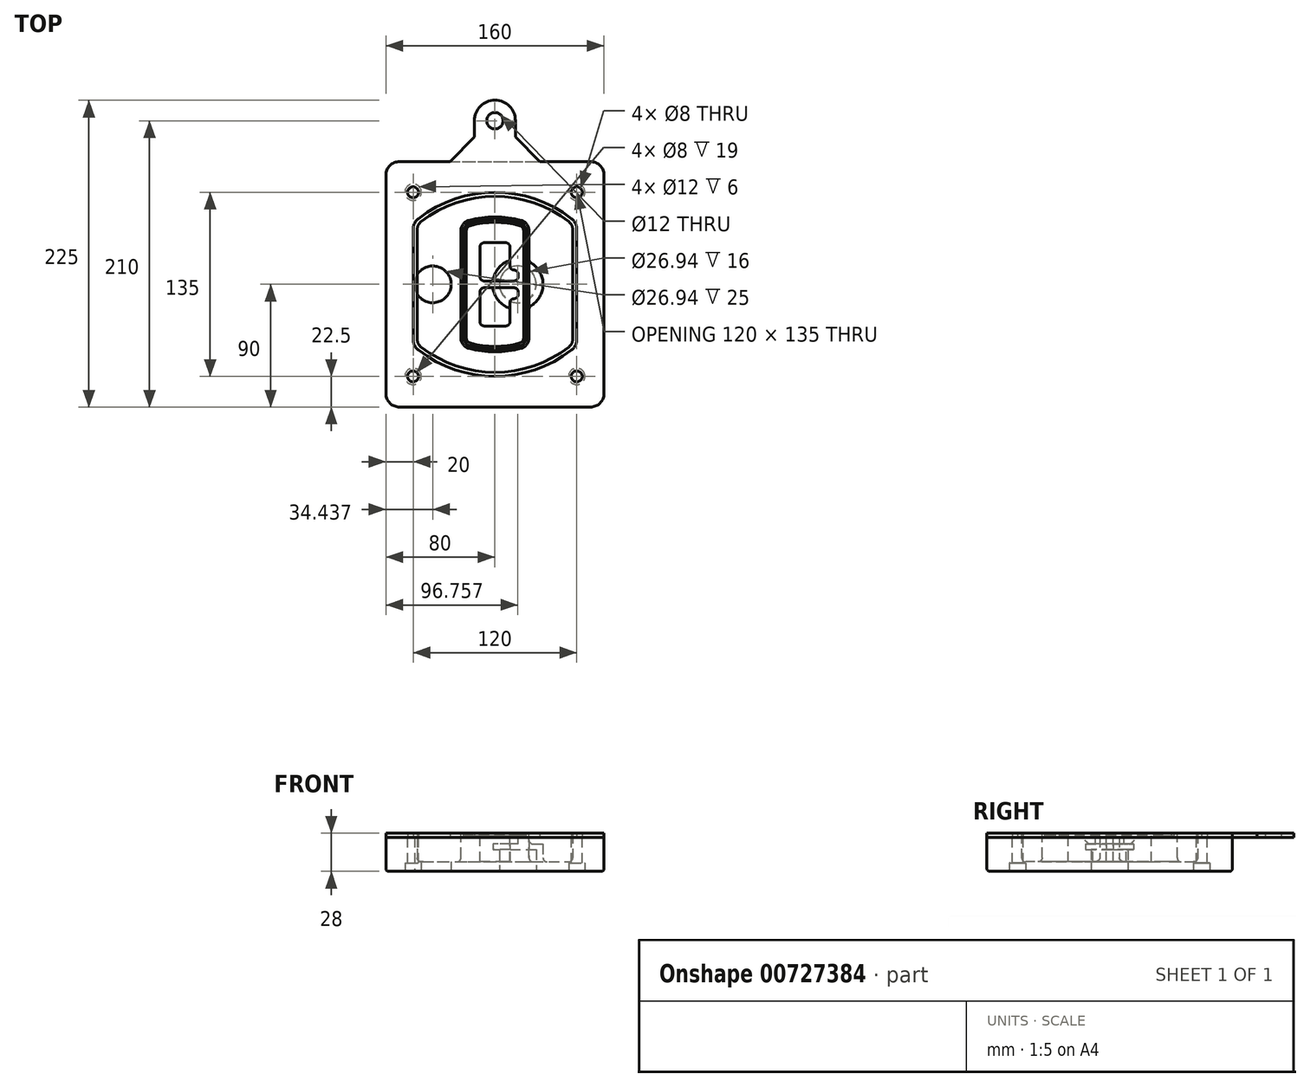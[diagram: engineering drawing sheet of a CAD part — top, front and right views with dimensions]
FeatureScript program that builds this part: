
annotation { "Feature Type Name" : "Feature", "Feature Type Description" : "" }
export const myFeature = defineFeature(function(context is Context, id is Id, definition is map)
    precondition{}
    {
        {
            var Q0;
            Q0=qCreatedBy(makeId("Top.planeOp"),FACE);
            var sketch = newSketch(context, id + "F0", { "sketchPlane" : qUnion([Q0])});
            skPoint(sketch, "E0.rect.middle", {"position": v(0, 0) * mm});
            skLineSegment(sketch, "E1.bottom", {"start": v(-70, -90) * mm, "end": v(70, -90) * mm});
            skLineSegment(sketch, "E1.top", {"start": v(-70, 90) * mm, "end": v(70, 90) * mm});
            skLineSegment(sketch, "E1.left", {"start": v(-80, -80) * mm, "end": v(-80, 80) * mm});
            skLineSegment(sketch, "E1.right", {"start": v(80, -80) * mm, "end": v(80, 80) * mm});
            skLineSegment(sketch, "E2", {"start": v(-80, 90) * mm, "end": v(80, -90) * mm, "construction": true});
            skLineSegment(sketch, "E3", {"start": v(80, 90) * mm, "end": v(-80, -90) * mm, "construction": true});
            skCircle(sketch, "E4", {"center": v(-60, 67.5) * mm, "radius": 4 * mm});
            skCircle(sketch, "E5", {"center": v(60, 67.5) * mm, "radius": 4 * mm});
            skCircle(sketch, "E6", {"center": v(60, -67.5) * mm, "radius": 4 * mm});
            skCircle(sketch, "E7", {"center": v(-60, -67.5) * mm, "radius": 4 * mm});
            skLineSegment(sketch, "E8", {"start": v(-60, 67.5) * mm, "end": v(60, 67.5) * mm, "construction": true});
            skLineSegment(sketch, "E9", {"start": v(60, 67.5) * mm, "end": v(60, -67.5) * mm, "construction": true});
            skLineSegment(sketch, "E10", {"start": v(60, -67.5) * mm, "end": v(-60, -67.5) * mm, "construction": true});
            skLineSegment(sketch, "E11", {"start": v(-60, -67.5) * mm, "end": v(-60, 67.5) * mm, "construction": true});
            skLineSegment(sketch, "E12", {"start": v(-60, 40.3) * mm, "end": v(-60, -40.3) * mm});
            skLineSegment(sketch, "E13", {"start": v(60, 40.3) * mm, "end": v(60, -40.3) * mm});
            skArc(sketch, "E14", {"start": v(56.15, 48.18) * mm, "mid": v(0, 67.5) * mm, "end": v(-56.15, 48.18) * mm});
            skArc(sketch, "E15", {"start": v(-56.15, -48.18) * mm, "mid": v(0, -67.5) * mm, "end": v(56.15, -48.18) * mm});
            skLineSegment(sketch, "E16", {"start": v(-60, 0) * mm, "end": v(60, 0) * mm, "construction": true});
            skPoint(sketch, "E17.visualSharp", {"position": v(-60, -45) * mm});
            skArc(sketch, "E17.filletArc", {"start": v(-60, -40.3) * mm, "mid": v(-58.99, -44.68) * mm, "end": v(-56.15, -48.18) * mm});
            skPoint(sketch, "E18.visualSharp", {"position": v(-60, 45) * mm});
            skArc(sketch, "E18.filletArc", {"start": v(-56.15, 48.18) * mm, "mid": v(-58.99, 44.68) * mm, "end": v(-60, 40.3) * mm});
            skPoint(sketch, "E19.visualSharp", {"position": v(60, 45) * mm});
            skArc(sketch, "E19.filletArc", {"start": v(60, 40.3) * mm, "mid": v(58.99, 44.68) * mm, "end": v(56.15, 48.18) * mm});
            skPoint(sketch, "E20.visualSharp", {"position": v(60, -45) * mm});
            skArc(sketch, "E20.filletArc", {"start": v(56.15, -48.18) * mm, "mid": v(58.99, -44.68) * mm, "end": v(60, -40.3) * mm});
            skPoint(sketch, "E21.visualSharp", {"position": v(-80, 90) * mm});
            skArc(sketch, "E21.filletArc", {"start": v(-70, 90) * mm, "mid": v(-77.07, 87.07) * mm, "end": v(-80, 80) * mm});
            skPoint(sketch, "E22.visualSharp", {"position": v(80, 90) * mm});
            skArc(sketch, "E22.filletArc", {"start": v(80, 80) * mm, "mid": v(77.07, 87.07) * mm, "end": v(70, 90) * mm});
            skPoint(sketch, "E23.visualSharp", {"position": v(80, -90) * mm});
            skArc(sketch, "E23.filletArc", {"start": v(70, -90) * mm, "mid": v(77.07, -87.07) * mm, "end": v(80, -80) * mm});
            skPoint(sketch, "E24.visualSharp", {"position": v(-80, -90) * mm});
            skArc(sketch, "E24.filletArc", {"start": v(-80, -80) * mm, "mid": v(-77.07, -87.07) * mm, "end": v(-70, -90) * mm});
            skArc(sketch, "E25.0", {"start": v(57, 40.3) * mm, "mid": v(56.3, 43.36) * mm, "end": v(54.3, 45.81) * mm});
            skLineSegment(sketch, "E25.1", {"start": v(57, 40.3) * mm, "end": v(57, -40.3) * mm});
            skArc(sketch, "E25.2", {"start": v(54.3, -45.81) * mm, "mid": v(56.3, -43.36) * mm, "end": v(57, -40.3) * mm});
            skArc(sketch, "E25.3", {"start": v(-54.3, -45.81) * mm, "mid": v(0, -64.5) * mm, "end": v(54.3, -45.81) * mm});
            skArc(sketch, "E25.4", {"start": v(-57, -40.3) * mm, "mid": v(-56.3, -43.36) * mm, "end": v(-54.3, -45.81) * mm});
            skArc(sketch, "E25.5", {"start": v(54.3, 45.81) * mm, "mid": v(0, 64.5) * mm, "end": v(-54.3, 45.81) * mm});
            skLineSegment(sketch, "E25.6", {"start": v(-57, 40.3) * mm, "end": v(-57, -40.3) * mm});
            skArc(sketch, "E25.7", {"start": v(-54.3, 45.81) * mm, "mid": v(-56.3, 43.36) * mm, "end": v(-57, 40.3) * mm});
            skArc(sketch, "E26.0", {"start": v(-58.62, 51.33) * mm, "mid": v(-62.58, 46.43) * mm, "end": v(-64, 40.3) * mm});
            skArc(sketch, "E26.1", {"start": v(58.62, 51.33) * mm, "mid": v(0, 71.5) * mm, "end": v(-58.62, 51.33) * mm});
            skArc(sketch, "E26.2", {"start": v(64, 40.3) * mm, "mid": v(62.58, 46.43) * mm, "end": v(58.62, 51.33) * mm});
            skLineSegment(sketch, "E26.3", {"start": v(64, 40.3) * mm, "end": v(64, -40.3) * mm});
            skArc(sketch, "E26.4", {"start": v(58.62, -51.33) * mm, "mid": v(62.58, -46.43) * mm, "end": v(64, -40.3) * mm});
            skLineSegment(sketch, "E26.5", {"start": v(-64, 40.3) * mm, "end": v(-64, -40.3) * mm});
            skArc(sketch, "E26.6", {"start": v(-58.62, -51.33) * mm, "mid": v(0, -71.5) * mm, "end": v(58.62, -51.33) * mm});
            skArc(sketch, "E26.7", {"start": v(-64, -40.3) * mm, "mid": v(-62.58, -46.43) * mm, "end": v(-58.62, -51.33) * mm});
            skSolve(sketch);
        }
        {
            var Q0;
            Q0=makeQuery(id+"F0.imprint","IMPRINT",FACE,{"disambiguationData":[TD([[makeQuery(id+"F0.imprint","IMPRINT",EDGE,{"derivedFrom":sQuery(id+"F0.wireOp",EDGE,"E1.bottom")}),1.0]])]});
            var Q1;
            Q1=makeQuery(id+"F0.imprint","IMPRINT",FACE,{"disambiguationData":[TD([[makeQuery(id+"F0.imprint","IMPRINT",EDGE,{"derivedFrom":sQuery(id+"F0.wireOp",EDGE,"E12")}),1.0]])]});
            var Q2;
            Q2=makeQuery(id+"F0.imprint","IMPRINT",FACE,{"disambiguationData":[TD([[makeQuery(id+"F0.imprint","IMPRINT",EDGE,{"derivedFrom":sQuery(id+"F0.wireOp",EDGE,"E25.0")}),1.0]])]});
            var Q3;
            Q3=makeQuery(id+"F0.imprint","IMPRINT",FACE,{"disambiguationData":[TD([[makeQuery(id+"F0.imprint","IMPRINT",EDGE,{"derivedFrom":sQuery(id+"F0.wireOp",EDGE,"E12")}),-1.0]])]});
            extrude(context, id + "F1", {"entities" : qUnion([Q0, Q1, Q2, Q3]), "oppositeDirection" : true, "depth" : 25 * mm});
        }
        {
            var Q0;
            Q0=makeQuery(id+"F0.imprint","IMPRINT",FACE,{"disambiguationData":[TD([[makeQuery(id+"F0.imprint","IMPRINT",EDGE,{"derivedFrom":sQuery(id+"F0.wireOp",EDGE,"E12")}),1.0]])]});
            extrude(context, id + "F2", {"entities" : qUnion([Q0]), "operationType" : NewBodyOperationType.ADD, "depth" : 3 * mm});
        }
        {
            var Q0;
            Q0=makeQuery(id+"F0.imprint","IMPRINT",FACE,{"disambiguationData":[TD([[makeQuery(id+"F0.imprint","IMPRINT",EDGE,{"derivedFrom":sQuery(id+"F0.wireOp",EDGE,"E25.0")}),1.0]])]});
            extrude(context, id + "F3", {"entities" : qUnion([Q0]), "operationType" : NewBodyOperationType.REMOVE, "oppositeDirection" : true, "depth" : 18 * mm});
        }
        {
            var Q0;
            Q0=makeQuery(id+"F2.opExtrude","CAP_FACE",FACE,{"disambiguationData":[OSD([sQuery(id+"F0.wireOp",EDGE,"E12"),sQuery(id+"F0.wireOp",EDGE,"E13"),sQuery(id+"F0.wireOp",EDGE,"E14"),sQuery(id+"F0.wireOp",EDGE,"E15"),sQuery(id+"F0.wireOp",EDGE,"E17.filletArc"),sQuery(id+"F0.wireOp",EDGE,"E18.filletArc"),sQuery(id+"F0.wireOp",EDGE,"E19.filletArc"),sQuery(id+"F0.wireOp",EDGE,"E20.filletArc"),sQuery(id+"F0.wireOp",EDGE,"E25.0"),sQuery(id+"F0.wireOp",EDGE,"E25.1"),sQuery(id+"F0.wireOp",EDGE,"E25.2"),sQuery(id+"F0.wireOp",EDGE,"E25.3"),sQuery(id+"F0.wireOp",EDGE,"E25.4"),sQuery(id+"F0.wireOp",EDGE,"E25.5"),sQuery(id+"F0.wireOp",EDGE,"E25.6"),sQuery(id+"F0.wireOp",EDGE,"E25.7")])],"isStart":false});
            var sketch = newSketch(context, id + "F4", { "sketchPlane" : qUnion([Q0])});
            skArc(sketch, "E27.0", {"start": v(-19.08, -46.97) * mm, "mid": v(0, -49.5) * mm, "end": v(19.08, -46.97) * mm});
            skArc(sketch, "E28.0", {"start": v(19.08, 46.97) * mm, "mid": v(0, 49.5) * mm, "end": v(-19.08, 46.97) * mm});
            skLineSegment(sketch, "E29", {"start": v(-25, 39.25) * mm, "end": v(-25, -39.25) * mm});
            skLineSegment(sketch, "E30", {"start": v(25, 39.25) * mm, "end": v(25, -39.25) * mm});
            skLineSegment(sketch, "E31", {"start": v(-25, 45.1) * mm, "end": v(25, 45.1) * mm, "construction": true});
            skLineSegment(sketch, "E32", {"start": v(-25, -45.1) * mm, "end": v(25, -45.1) * mm, "construction": true});
            skPoint(sketch, "E33.visualSharp", {"position": v(-25, 45.1) * mm});
            skArc(sketch, "E33.filletArc", {"start": v(-19.08, 46.97) * mm, "mid": v(-23.35, 44.11) * mm, "end": v(-25, 39.25) * mm});
            skPoint(sketch, "E34.visualSharp", {"position": v(25, 45.1) * mm});
            skArc(sketch, "E34.filletArc", {"start": v(25, 39.25) * mm, "mid": v(23.35, 44.11) * mm, "end": v(19.08, 46.97) * mm});
            skPoint(sketch, "E35.visualSharp", {"position": v(25, -45.1) * mm});
            skArc(sketch, "E35.filletArc", {"start": v(19.08, -46.97) * mm, "mid": v(23.35, -44.11) * mm, "end": v(25, -39.25) * mm});
            skPoint(sketch, "E36.visualSharp", {"position": v(-25, -45.1) * mm});
            skArc(sketch, "E36.filletArc", {"start": v(-25, -39.25) * mm, "mid": v(-23.35, -44.11) * mm, "end": v(-19.08, -46.97) * mm});
            skArc(sketch, "E37.0", {"start": v(54.3, 45.81) * mm, "mid": v(0, 64.5) * mm, "end": v(-54.3, 45.81) * mm});
            skArc(sketch, "E37.1", {"start": v(-54.3, 45.81) * mm, "mid": v(-56.3, 43.36) * mm, "end": v(-57, 40.3) * mm});
            skLineSegment(sketch, "E37.2", {"start": v(-57, 40.3) * mm, "end": v(-57, -40.3) * mm});
            skArc(sketch, "E37.3", {"start": v(-57, -40.3) * mm, "mid": v(-56.3, -43.36) * mm, "end": v(-54.3, -45.81) * mm});
            skArc(sketch, "E37.4", {"start": v(-54.3, -45.81) * mm, "mid": v(0, -64.5) * mm, "end": v(54.3, -45.81) * mm});
            skArc(sketch, "E37.5", {"start": v(54.3, -45.81) * mm, "mid": v(56.3, -43.36) * mm, "end": v(57, -40.3) * mm});
            skLineSegment(sketch, "E37.6", {"start": v(57, 40.3) * mm, "end": v(57, -40.3) * mm});
            skArc(sketch, "E37.7", {"start": v(57, 40.3) * mm, "mid": v(56.3, 43.36) * mm, "end": v(54.3, 45.81) * mm});
            skLineSegment(sketch, "E38.0", {"start": v(23, 39.25) * mm, "end": v(23, -39.25) * mm});
            skArc(sketch, "E38.1", {"start": v(18.56, -45.04) * mm, "mid": v(21.76, -42.9) * mm, "end": v(23, -39.25) * mm});
            skArc(sketch, "E38.2", {"start": v(-18.56, -45.04) * mm, "mid": v(0, -47.5) * mm, "end": v(18.56, -45.04) * mm});
            skArc(sketch, "E38.3", {"start": v(-23, -39.25) * mm, "mid": v(-21.76, -42.9) * mm, "end": v(-18.56, -45.04) * mm});
            skLineSegment(sketch, "E38.4", {"start": v(-23, 39.25) * mm, "end": v(-23, -39.25) * mm});
            skArc(sketch, "E38.5", {"start": v(23, 39.25) * mm, "mid": v(21.76, 42.9) * mm, "end": v(18.56, 45.04) * mm});
            skArc(sketch, "E38.6", {"start": v(-18.56, 45.04) * mm, "mid": v(-21.76, 42.9) * mm, "end": v(-23, 39.25) * mm});
            skArc(sketch, "E38.7", {"start": v(18.56, 45.04) * mm, "mid": v(0, 47.5) * mm, "end": v(-18.56, 45.04) * mm});
            skArc(sketch, "E39.0", {"start": v(21, 39.25) * mm, "mid": v(20.18, 41.68) * mm, "end": v(18.04, 43.1) * mm});
            skLineSegment(sketch, "E39.1", {"start": v(21, 39.25) * mm, "end": v(21, -39.25) * mm});
            skArc(sketch, "E39.2", {"start": v(18.04, -43.1) * mm, "mid": v(20.18, -41.68) * mm, "end": v(21, -39.25) * mm});
            skArc(sketch, "E39.3", {"start": v(-18.04, -43.1) * mm, "mid": v(0, -45.5) * mm, "end": v(18.04, -43.1) * mm});
            skArc(sketch, "E39.4", {"start": v(-21, -39.25) * mm, "mid": v(-20.18, -41.68) * mm, "end": v(-18.04, -43.1) * mm});
            skArc(sketch, "E39.5", {"start": v(18.04, 43.1) * mm, "mid": v(0, 45.5) * mm, "end": v(-18.04, 43.1) * mm});
            skLineSegment(sketch, "E39.6", {"start": v(-21, 39.25) * mm, "end": v(-21, -39.25) * mm});
            skArc(sketch, "E39.7", {"start": v(-18.04, 43.1) * mm, "mid": v(-20.18, 41.68) * mm, "end": v(-21, 39.25) * mm});
            skLineSegment(sketch, "E40", {"start": v(-25, 0) * mm, "end": v(25, 0) * mm, "construction": true});
            skLineSegment(sketch, "E41", {"start": v(-11, 5.5) * mm, "end": v(-11, 27.5) * mm});
            skLineSegment(sketch, "E42", {"start": v(-8, 30.5) * mm, "end": v(8, 30.5) * mm});
            skLineSegment(sketch, "E43", {"start": v(11, 27.5) * mm, "end": v(11, 13.5) * mm});
            skLineSegment(sketch, "E44", {"start": v(14, 10.5) * mm, "end": v(14, 10.5) * mm});
            skLineSegment(sketch, "E45", {"start": v(17, 7.5) * mm, "end": v(17, 5.5) * mm});
            skLineSegment(sketch, "E46", {"start": v(14, 2.5) * mm, "end": v(-8, 2.5) * mm});
            skPoint(sketch, "E47.visualSharp", {"position": v(-11, 30.5) * mm});
            skArc(sketch, "E47.filletArc", {"start": v(-8, 30.5) * mm, "mid": v(-10.12, 29.62) * mm, "end": v(-11, 27.5) * mm});
            skPoint(sketch, "E48.visualSharp", {"position": v(11, 30.5) * mm});
            skArc(sketch, "E48.filletArc", {"start": v(11, 27.5) * mm, "mid": v(10.12, 29.62) * mm, "end": v(8, 30.5) * mm});
            skPoint(sketch, "E49.visualSharp", {"position": v(11, 10.5) * mm});
            skArc(sketch, "E49.filletArc", {"start": v(11, 13.5) * mm, "mid": v(11.88, 11.38) * mm, "end": v(14, 10.5) * mm});
            skPoint(sketch, "E50.visualSharp", {"position": v(17, 10.5) * mm});
            skArc(sketch, "E50.filletArc", {"start": v(17, 7.5) * mm, "mid": v(16.12, 9.62) * mm, "end": v(14, 10.5) * mm});
            skPoint(sketch, "E51.visualSharp", {"position": v(17, 2.5) * mm});
            skArc(sketch, "E51.filletArc", {"start": v(14, 2.5) * mm, "mid": v(16.12, 3.38) * mm, "end": v(17, 5.5) * mm});
            skPoint(sketch, "E52.visualSharp", {"position": v(-11, 2.5) * mm});
            skArc(sketch, "E52.filletArc", {"start": v(-11, 5.5) * mm, "mid": v(-10.12, 3.38) * mm, "end": v(-8, 2.5) * mm});
            skLineSegment(sketch, "E53.0.MirrorCS", {"start": v(14, -2.5) * mm, "end": v(-8, -2.5) * mm});
            skArc(sketch, "E54.0.MirrorCS", {"start": v(-11, -5.5) * mm, "mid": v(-10.12, -3.38) * mm, "end": v(-8, -2.5) * mm});
            skLineSegment(sketch, "E55.0.MirrorCS", {"start": v(-11, -5.5) * mm, "end": v(-11, -27.5) * mm});
            skArc(sketch, "E56.0.MirrorCS", {"start": v(-8, -30.5) * mm, "mid": v(-10.12, -29.62) * mm, "end": v(-11, -27.5) * mm});
            skLineSegment(sketch, "E57.0.MirrorCS", {"start": v(-8, -30.5) * mm, "end": v(8, -30.5) * mm});
            skArc(sketch, "E58.0.MirrorCS", {"start": v(11, -27.5) * mm, "mid": v(10.12, -29.62) * mm, "end": v(8, -30.5) * mm});
            skLineSegment(sketch, "E59.0.MirrorCS", {"start": v(11, -27.5) * mm, "end": v(11, -13.5) * mm});
            skArc(sketch, "E60.0.MirrorCS", {"start": v(11, -13.5) * mm, "mid": v(11.88, -11.38) * mm, "end": v(14, -10.5) * mm});
            skArc(sketch, "E61.0.MirrorCS", {"start": v(17, -7.5) * mm, "mid": v(16.12, -9.62) * mm, "end": v(14, -10.5) * mm});
            skLineSegment(sketch, "E62.0.MirrorCS", {"start": v(17, -7.5) * mm, "end": v(17, -5.5) * mm});
            skArc(sketch, "E63.0.MirrorCS", {"start": v(14, -2.5) * mm, "mid": v(16.12, -3.38) * mm, "end": v(17, -5.5) * mm});
            skSolve(sketch);
        }
        {
            var Q0;
            Q0=makeQuery(id+"F4.imprint","IMPRINT",FACE,{"disambiguationData":[TD([[makeQuery(id+"F4.imprint","IMPRINT",EDGE,{"derivedFrom":sQuery(id+"F4.wireOp",EDGE,"E27.0")}),1.0]])]});
            var Q1;
            Q1=makeQuery(id+"F4.imprint","IMPRINT",FACE,{"disambiguationData":[TD([[makeQuery(id+"F4.imprint","IMPRINT",EDGE,{"derivedFrom":sQuery(id+"F4.wireOp",EDGE,"E38.0")}),-1.0]])]});
            var Q2;
            Q2=makeQuery(id+"F4.imprint","IMPRINT",FACE,{"disambiguationData":[TD([[makeQuery(id+"F4.imprint","IMPRINT",EDGE,{"derivedFrom":sQuery(id+"F4.wireOp",EDGE,"E39.0")}),1.0]])]});
            extrude(context, id + "F5", {"entities" : qUnion([Q0, Q1, Q2]), "operationType" : NewBodyOperationType.ADD, "endBound" : BoundingType.UP_TO_NEXT, "oppositeDirection" : true, "depth" : 25 * mm});
        }
        {
            var Q0;
            Q0=makeQuery(id+"F4.imprint","IMPRINT",FACE,{"disambiguationData":[TD([[makeQuery(id+"F4.imprint","IMPRINT",EDGE,{"derivedFrom":sQuery(id+"F4.wireOp",EDGE,"E38.0")}),-1.0]])]});
            extrude(context, id + "F6", {"entities" : qUnion([Q0]), "operationType" : NewBodyOperationType.REMOVE, "oppositeDirection" : true, "depth" : 2 * mm});
        }
        {
            var Q0;
            Q0=makeQuery(id+"F1.opExtrude","CAP_FACE",FACE,{"disambiguationData":[OSD([sQuery(id+"F0.wireOp",EDGE,"E1.bottom"),sQuery(id+"F0.wireOp",EDGE,"E1.top"),sQuery(id+"F0.wireOp",EDGE,"E1.left"),sQuery(id+"F0.wireOp",EDGE,"E1.right"),sQuery(id+"F0.wireOp",EDGE,"E4"),sQuery(id+"F0.wireOp",EDGE,"E5"),sQuery(id+"F0.wireOp",EDGE,"E6"),sQuery(id+"F0.wireOp",EDGE,"E7"),sQuery(id+"F0.wireOp",EDGE,"E21.filletArc"),sQuery(id+"F0.wireOp",EDGE,"E22.filletArc"),sQuery(id+"F0.wireOp",EDGE,"E23.filletArc"),sQuery(id+"F0.wireOp",EDGE,"E24.filletArc")])],"isStart":false});
            var sketch = newSketch(context, id + "F7", { "sketchPlane" : qUnion([Q0])});
            skCircle(sketch, "E64", {"center": v(16.76, 0) * mm, "radius": 13.47 * mm});
            skCircle(sketch, "E65", {"center": v(-45.56, 0) * mm, "radius": 13.47 * mm});
            skLineSegment(sketch, "E66", {"start": v(80, 0) * mm, "end": v(-80, 0) * mm});
            skCircle(sketch, "E67", {"center": v(16.76, 0) * mm, "radius": 18.47 * mm});
            skCircle(sketch, "E68", {"center": v(60, -67.5) * mm, "radius": 6 * mm});
            skCircle(sketch, "E69", {"center": v(-60, -67.5) * mm, "radius": 6 * mm});
            skCircle(sketch, "E70", {"center": v(-60, 67.5) * mm, "radius": 6 * mm});
            skCircle(sketch, "E71", {"center": v(60, 67.5) * mm, "radius": 6 * mm});
            skSolve(sketch);
        }
        {
            var Q0;
            {var subQ1=sQuery(id+"F7.wireOp",EDGE,"E66");var subQ4=sQuery(id+"F7.wireOp",EDGE,"E64");var subQ6=makeQuery(id+"F7.imprint","INTERSECT",VERTEX,{"disambiguationData":[OD(0.0)],"derivedFrom":[subQ4,subQ1]});Q0=makeQuery(id+"F7.imprint","IMPRINT",FACE,{"disambiguationData":[TD([[makeQuery(id+"F7.imprint","IMPRINT",EDGE,{"disambiguationData":[TD([[subQ6,-1.0]])],"derivedFrom":subQ4}),-1.0]])]});}
            var Q1;
            {var subQ0=sQuery(id+"F7.wireOp",EDGE,"E66");var subQ1=sQuery(id+"F7.wireOp",EDGE,"E64");var subQ3=makeQuery(id+"F7.imprint","INTERSECT",VERTEX,{"disambiguationData":[OD(0.0)],"derivedFrom":[subQ1,subQ0]});Q1=makeQuery(id+"F7.imprint","IMPRINT",FACE,{"disambiguationData":[TD([[makeQuery(id+"F7.imprint","IMPRINT",EDGE,{"disambiguationData":[TD([[subQ3,-1.0]])],"derivedFrom":subQ1}),1.0]])]});}
            var Q2;
            {var subQ0=sQuery(id+"F7.wireOp",EDGE,"E66");var subQ1=sQuery(id+"F7.wireOp",EDGE,"E64");var subQ3=makeQuery(id+"F7.imprint","INTERSECT",VERTEX,{"disambiguationData":[OD(0.0)],"derivedFrom":[subQ1,subQ0]});Q2=makeQuery(id+"F7.imprint","IMPRINT",FACE,{"disambiguationData":[TD([[makeQuery(id+"F7.imprint","IMPRINT",EDGE,{"disambiguationData":[TD([[subQ3,1.0]])],"derivedFrom":subQ1}),1.0]])]});}
            var Q3;
            {var subQ1=sQuery(id+"F7.wireOp",EDGE,"E66");var subQ4=sQuery(id+"F7.wireOp",EDGE,"E64");var subQ6=makeQuery(id+"F7.imprint","INTERSECT",VERTEX,{"disambiguationData":[OD(0.0)],"derivedFrom":[subQ4,subQ1]});Q3=makeQuery(id+"F7.imprint","IMPRINT",FACE,{"disambiguationData":[TD([[makeQuery(id+"F7.imprint","IMPRINT",EDGE,{"disambiguationData":[TD([[subQ6,1.0]])],"derivedFrom":subQ4}),-1.0]])]});}
            extrude(context, id + "F8", {"entities" : qUnion([Q0, Q1, Q2, Q3]), "operationType" : NewBodyOperationType.ADD, "oppositeDirection" : true, "depth" : 20 * mm});
        }
        {
            var Q0;
            {var subQ0=sQuery(id+"F7.wireOp",EDGE,"E66");var subQ1=sQuery(id+"F7.wireOp",EDGE,"E64");var subQ3=makeQuery(id+"F7.imprint","INTERSECT",VERTEX,{"disambiguationData":[OD(0.0)],"derivedFrom":[subQ1,subQ0]});Q0=makeQuery(id+"F7.imprint","IMPRINT",FACE,{"disambiguationData":[TD([[makeQuery(id+"F7.imprint","IMPRINT",EDGE,{"disambiguationData":[TD([[subQ3,-1.0]])],"derivedFrom":subQ1}),1.0]])]});}
            var Q1;
            {var subQ0=sQuery(id+"F7.wireOp",EDGE,"E66");var subQ1=sQuery(id+"F7.wireOp",EDGE,"E64");var subQ3=makeQuery(id+"F7.imprint","INTERSECT",VERTEX,{"disambiguationData":[OD(0.0)],"derivedFrom":[subQ1,subQ0]});Q1=makeQuery(id+"F7.imprint","IMPRINT",FACE,{"disambiguationData":[TD([[makeQuery(id+"F7.imprint","IMPRINT",EDGE,{"disambiguationData":[TD([[subQ3,1.0]])],"derivedFrom":subQ1}),1.0]])]});}
            extrude(context, id + "F9", {"entities" : qUnion([Q0, Q1]), "operationType" : NewBodyOperationType.REMOVE, "oppositeDirection" : true, "depth" : 16 * mm});
        }
        {
            var Q0;
            {var subQ0=sQuery(id+"F7.wireOp",EDGE,"E66");var subQ1=sQuery(id+"F7.wireOp",EDGE,"E65");var subQ3=makeQuery(id+"F7.imprint","INTERSECT",VERTEX,{"disambiguationData":[OD(0.0)],"derivedFrom":[subQ1,subQ0]});Q0=makeQuery(id+"F7.imprint","IMPRINT",FACE,{"disambiguationData":[TD([[makeQuery(id+"F7.imprint","IMPRINT",EDGE,{"disambiguationData":[TD([[subQ3,-1.0]])],"derivedFrom":subQ1}),1.0]])]});}
            var Q1;
            {var subQ0=sQuery(id+"F7.wireOp",EDGE,"E66");var subQ1=sQuery(id+"F7.wireOp",EDGE,"E65");var subQ3=makeQuery(id+"F7.imprint","INTERSECT",VERTEX,{"disambiguationData":[OD(0.0)],"derivedFrom":[subQ1,subQ0]});Q1=makeQuery(id+"F7.imprint","IMPRINT",FACE,{"disambiguationData":[TD([[makeQuery(id+"F7.imprint","IMPRINT",EDGE,{"disambiguationData":[TD([[subQ3,1.0]])],"derivedFrom":subQ1}),1.0]])]});}
            extrude(context, id + "F10", {"entities" : qUnion([Q0, Q1]), "operationType" : NewBodyOperationType.REMOVE, "oppositeDirection" : true, "depth" : 25 * mm});
        }
        {
            var Q0;
            Q0=makeQuery(id+"F7.imprint","IMPRINT",FACE,{"disambiguationData":[TD([[makeQuery(id+"F7.imprint","IMPRINT",EDGE,{"derivedFrom":sQuery(id+"F7.wireOp",EDGE,"E68")}),1.0]])]});
            var Q1;
            Q1=makeQuery(id+"F7.imprint","IMPRINT",FACE,{"disambiguationData":[TD([[makeQuery(id+"F7.imprint","IMPRINT",EDGE,{"derivedFrom":makeQuery(id+"F1.opExtrude","CAP_EDGE",EDGE,{"disambiguationData":[OSD([sQuery(id+"F0.wireOp",EDGE,"E5")])],"isStart":false})}),-1.0]])]});
            var Q2;
            Q2=makeQuery(id+"F7.imprint","IMPRINT",FACE,{"disambiguationData":[TD([[makeQuery(id+"F7.imprint","IMPRINT",EDGE,{"derivedFrom":sQuery(id+"F7.wireOp",EDGE,"E69")}),1.0]])]});
            var Q3;
            Q3=makeQuery(id+"F7.imprint","IMPRINT",FACE,{"disambiguationData":[TD([[makeQuery(id+"F7.imprint","IMPRINT",EDGE,{"derivedFrom":makeQuery(id+"F1.opExtrude","CAP_EDGE",EDGE,{"disambiguationData":[OSD([sQuery(id+"F0.wireOp",EDGE,"E4")])],"isStart":false})}),-1.0]])]});
            var Q4;
            Q4=makeQuery(id+"F7.imprint","IMPRINT",FACE,{"disambiguationData":[TD([[makeQuery(id+"F7.imprint","IMPRINT",EDGE,{"derivedFrom":sQuery(id+"F7.wireOp",EDGE,"E70")}),1.0]])]});
            var Q5;
            Q5=makeQuery(id+"F7.imprint","IMPRINT",FACE,{"disambiguationData":[TD([[makeQuery(id+"F7.imprint","IMPRINT",EDGE,{"derivedFrom":makeQuery(id+"F1.opExtrude","CAP_EDGE",EDGE,{"disambiguationData":[OSD([sQuery(id+"F0.wireOp",EDGE,"E7")])],"isStart":false})}),-1.0]])]});
            var Q6;
            Q6=makeQuery(id+"F7.imprint","IMPRINT",FACE,{"disambiguationData":[TD([[makeQuery(id+"F7.imprint","IMPRINT",EDGE,{"derivedFrom":sQuery(id+"F7.wireOp",EDGE,"E71")}),1.0]])]});
            var Q7;
            Q7=makeQuery(id+"F7.imprint","IMPRINT",FACE,{"disambiguationData":[TD([[makeQuery(id+"F7.imprint","IMPRINT",EDGE,{"derivedFrom":makeQuery(id+"F1.opExtrude","CAP_EDGE",EDGE,{"disambiguationData":[OSD([sQuery(id+"F0.wireOp",EDGE,"E6")])],"isStart":false})}),-1.0]])]});
            extrude(context, id + "F11", {"entities" : qUnion([Q0, Q1, Q2, Q3, Q4, Q5, Q6, Q7]), "operationType" : NewBodyOperationType.REMOVE, "oppositeDirection" : true, "depth" : 6 * mm});
        }
        {
            var Q0;
            Q0=makeQuery(id+"F9.boolean.opBoolean","COPY",FACE,{"derivedFrom":makeQuery(id+"F9.opExtrude","CAP_FACE",FACE,{"disambiguationData":[OSD([sQuery(id+"F7.wireOp",EDGE,"E64")])],"isStart":false})});
            var sketch = newSketch(context, id + "F12", { "sketchPlane" : qUnion([Q0])});
            skArc(sketch, "E72.0", {"start": v(11, 17.55) * mm, "mid": v(2.57, 11.82) * mm, "end": v(-1.54, 2.5) * mm});
            skArc(sketch, "E72.1", {"start": v(-1.54, -2.5) * mm, "mid": v(2.57, -11.82) * mm, "end": v(11, -17.55) * mm});
            skLineSegment(sketch, "E73", {"start": v(-1.54, -2.5) * mm, "end": v(14, -2.5) * mm});
            skLineSegment(sketch, "E74.0", {"start": v(14, 2.5) * mm, "end": v(-1.54, 2.5) * mm});
            skArc(sketch, "E74.1", {"start": v(14, 2.5) * mm, "mid": v(16.12, 3.38) * mm, "end": v(17, 5.5) * mm});
            skLineSegment(sketch, "E74.2", {"start": v(17, 7.5) * mm, "end": v(17, 5.5) * mm});
            skArc(sketch, "E74.3", {"start": v(17, 7.5) * mm, "mid": v(16.12, 9.62) * mm, "end": v(14, 10.5) * mm});
            skArc(sketch, "E74.4", {"start": v(11, 13.5) * mm, "mid": v(11.88, 11.38) * mm, "end": v(14, 10.5) * mm});
            skLineSegment(sketch, "E74.5", {"start": v(11, 17.55) * mm, "end": v(11, 13.5) * mm});
            skLineSegment(sketch, "E74.7", {"start": v(14, -2.5) * mm, "end": v(-1.54, -2.5) * mm});
            skArc(sketch, "E74.8", {"start": v(14, -2.5) * mm, "mid": v(16.12, -3.38) * mm, "end": v(17, -5.5) * mm});
            skLineSegment(sketch, "E74.9", {"start": v(17, -7.5) * mm, "end": v(17, -5.5) * mm});
            skArc(sketch, "E74.10", {"start": v(17, -7.5) * mm, "mid": v(16.12, -9.62) * mm, "end": v(14, -10.5) * mm});
            skArc(sketch, "E74.11", {"start": v(11, -13.5) * mm, "mid": v(11.88, -11.38) * mm, "end": v(14, -10.5) * mm});
            skLineSegment(sketch, "E74.12", {"start": v(11, -17.55) * mm, "end": v(11, -13.5) * mm});
            skPoint(sketch, "E75.orphan", {"position": v(11, -27.5) * mm});
            skPoint(sketch, "E76.orphan", {"position": v(-8, -2.5) * mm});
            skPoint(sketch, "E77.orphan", {"position": v(-8, 2.5) * mm});
            skPoint(sketch, "E78.orphan", {"position": v(11, 27.5) * mm});
            skSolve(sketch);
        }
        {
            var Q0;
            {var subQ7=sQuery(id+"F12.wireOp",EDGE,"E72.0");var subQ14=sQuery(id+"F12.wireOp",EDGE,"E72.1");var subQ16=sQuery(id+"F12.wireOp",EDGE,"E74.1");var subQ18=sQuery(id+"F12.wireOp",EDGE,"E74.8");Q0=qUnion([makeQuery(id+"F12.imprint","IMPRINT",FACE,{"disambiguationData":[TD([[makeQuery(id+"F12.imprint","IMPRINT",EDGE,{"derivedFrom":subQ7}),1.0]])]}),makeQuery(id+"F12.imprint","IMPRINT",FACE,{"disambiguationData":[TD([[makeQuery(id+"F12.imprint","IMPRINT",EDGE,{"derivedFrom":subQ14}),1.0]])]}),makeQuery(id+"F12.imprint","IMPRINT",FACE,{"disambiguationData":[TD([[makeQuery(id+"F12.imprint","IMPRINT",EDGE,{"derivedFrom":subQ16}),1.0]])]}),makeQuery(id+"F12.imprint","IMPRINT",FACE,{"disambiguationData":[TD([[makeQuery(id+"F12.imprint","IMPRINT",EDGE,{"derivedFrom":subQ18}),-1.0]])]})]);}
            var Q1;
            Q1=makeQuery(id+"F5.boolean.opBoolean","SPLIT",FACE,{"disambiguationData":[TD([makeQuery(id+"F5.opExtrude","SWEPT_FACE",FACE,{"disambiguationData":[OSD([sQuery(id+"F4.wireOp",EDGE,"E41")])]})])],"derivedFrom":makeQuery(id+"F3.boolean.opBoolean","COPY",FACE,{"derivedFrom":makeQuery(id+"F3.opExtrude","CAP_FACE",FACE,{"disambiguationData":[OSD([sQuery(id+"F0.wireOp",EDGE,"E25.0"),sQuery(id+"F0.wireOp",EDGE,"E25.1"),sQuery(id+"F0.wireOp",EDGE,"E25.2"),sQuery(id+"F0.wireOp",EDGE,"E25.3"),sQuery(id+"F0.wireOp",EDGE,"E25.4"),sQuery(id+"F0.wireOp",EDGE,"E25.5"),sQuery(id+"F0.wireOp",EDGE,"E25.6"),sQuery(id+"F0.wireOp",EDGE,"E25.7")])],"isStart":false})})});
            extrude(context, id + "F13", {"entities" : qUnion([Q0]), "operationType" : NewBodyOperationType.REMOVE, "endBound" : BoundingType.UP_TO_SURFACE, "endBoundEntityFace" : qUnion([Q1]), "depth" : 25 * mm});
        }
        {
            var Q0;
            Q0=makeQuery(id+"F3.boolean.opBoolean","COPY",EDGE,{"derivedFrom":makeQuery(id+"F3.opExtrude","CAP_EDGE",EDGE,{"disambiguationData":[OSD([sQuery(id+"F0.wireOp",EDGE,"E25.6")])],"isStart":false})});
            var Q1;
            Q1=makeQuery(id+"F8.boolean.opBoolean","INTERSECT",EDGE,{"derivedFrom":[makeQuery(id+"F5.opExtrude","SWEPT_FACE",FACE,{"disambiguationData":[OSD([sQuery(id+"F4.wireOp",EDGE,"E30")])]}),makeQuery(id+"F8.opExtrude","CAP_FACE",FACE,{"disambiguationData":[OSD([sQuery(id+"F7.wireOp",EDGE,"E67")])],"isStart":false})]});
            var Q2;
            Q2=makeQuery(id+"F8.boolean.opBoolean","INTERSECT",EDGE,{"disambiguationData":[OD(1.0)],"derivedFrom":[makeQuery(id+"F5.opExtrude","SWEPT_FACE",FACE,{"disambiguationData":[OSD([sQuery(id+"F4.wireOp",EDGE,"E30")])]}),makeQuery(id+"F8.opExtrude","SWEPT_FACE",FACE,{"disambiguationData":[OSD([sQuery(id+"F7.wireOp",EDGE,"E67")])]})]});
            var Q3;
            {var subQ0=sQuery(id+"F4.wireOp",EDGE,"E30");Q3=makeQuery(id+"F8.boolean.opBoolean","SPLIT",EDGE,{"disambiguationData":[TD([makeQuery(id+"F5.opExtrude","SWEPT_FACE",FACE,{"disambiguationData":[OSD([sQuery(id+"F4.wireOp",EDGE,"E35.filletArc")])]})])],"derivedFrom":makeQuery(id+"F5.opExtrude","CAP_EDGE",EDGE,{"disambiguationData":[OSD([subQ0])],"isStart":false})});}
            var Q4;
            {var subQ0=sQuery(id+"F0.wireOp",EDGE,"E25.7");var subQ1=sQuery(id+"F0.wireOp",EDGE,"E25.1");var subQ2=sQuery(id+"F0.wireOp",EDGE,"E25.6");var subQ3=sQuery(id+"F0.wireOp",EDGE,"E25.5");var subQ4=sQuery(id+"F0.wireOp",EDGE,"E25.4");var subQ5=sQuery(id+"F0.wireOp",EDGE,"E25.0");var subQ6=sQuery(id+"F0.wireOp",EDGE,"E25.2");var subQ7=sQuery(id+"F0.wireOp",EDGE,"E25.3");Q4=makeQuery(id+"F8.boolean.opBoolean","INTERSECT",EDGE,{"derivedFrom":[makeQuery(id+"F5.boolean.opBoolean","SPLIT",FACE,{"disambiguationData":[TD([makeQuery(id+"F2.opExtrude","SWEPT_FACE",FACE,{"disambiguationData":[OSD([subQ5])]})])],"derivedFrom":makeQuery(id+"F3.boolean.opBoolean","COPY",FACE,{"derivedFrom":makeQuery(id+"F3.opExtrude","CAP_FACE",FACE,{"disambiguationData":[OSD([subQ5,subQ1,subQ6,subQ7,subQ4,subQ3,subQ2,subQ0])],"isStart":false})})}),makeQuery(id+"F8.opExtrude","SWEPT_FACE",FACE,{"disambiguationData":[OSD([sQuery(id+"F7.wireOp",EDGE,"E67")])]})]});}
            var Q5;
            Q5=makeQuery(id+"F8.boolean.opBoolean","INTERSECT",EDGE,{"disambiguationData":[OD(0.0)],"derivedFrom":[makeQuery(id+"F5.opExtrude","SWEPT_FACE",FACE,{"disambiguationData":[OSD([sQuery(id+"F4.wireOp",EDGE,"E30")])]}),makeQuery(id+"F8.opExtrude","SWEPT_FACE",FACE,{"disambiguationData":[OSD([sQuery(id+"F7.wireOp",EDGE,"E67")])]})]});
            fillet(context, id + "F14", {"entities" : qUnion([Q0, Q1, Q2, Q3, Q4, Q5]), "radius" : 3 * mm, "tangentPropagation" : true, "allowEdgeOverflow" : false});
        }
        {
            var Q0;
            Q0=makeQuery(id+"F1.opExtrude","CAP_EDGE",EDGE,{"disambiguationData":[OSD([sQuery(id+"F0.wireOp",EDGE,"E1.bottom")])],"isStart":false});
            fillet(context, id + "F15", {"entities" : qUnion([Q0]), "radius" : 2 * mm, "tangentPropagation" : true, "allowEdgeOverflow" : false});
        }
        {
            var Q0;
            {var subQ0=sQuery(id+"F0.wireOp",EDGE,"E21.filletArc");var subQ1=sQuery(id+"F0.wireOp",EDGE,"E7");var subQ2=sQuery(id+"F0.wireOp",EDGE,"E6");var subQ3=sQuery(id+"F0.wireOp",EDGE,"E5");var subQ4=sQuery(id+"F0.wireOp",EDGE,"E4");var subQ5=sQuery(id+"F0.wireOp",EDGE,"E22.filletArc");var subQ6=sQuery(id+"F0.wireOp",EDGE,"E1.bottom");var subQ7=sQuery(id+"F0.wireOp",EDGE,"E1.right");var subQ8=sQuery(id+"F0.wireOp",EDGE,"E1.top");var subQ9=sQuery(id+"F0.wireOp",EDGE,"E1.left");var subQ10=sQuery(id+"F0.wireOp",EDGE,"E23.filletArc");var subQ11=sQuery(id+"F0.wireOp",EDGE,"E24.filletArc");Q0=makeQuery(id+"F2.boolean.opBoolean","SPLIT",FACE,{"disambiguationData":[TD([makeQuery(id+"F1.opExtrude","SWEPT_FACE",FACE,{"disambiguationData":[OSD([subQ6])]})])],"derivedFrom":makeQuery(id+"F1.opExtrude","CAP_FACE",FACE,{"disambiguationData":[OSD([subQ6,subQ8,subQ9,subQ7,subQ4,subQ3,subQ2,subQ1,subQ0,subQ5,subQ10,subQ11])],"isStart":true})});}
            var sketch = newSketch(context, id + "F16", { "sketchPlane" : qUnion([Q0])});
            skLineSegment(sketch, "E79.0", {"start": v(-80, -80) * mm, "end": v(-80, 80) * mm});
            skCircle(sketch, "E79.1", {"center": v(-60, 67.5) * mm, "radius": 4 * mm});
            skLineSegment(sketch, "E79.2", {"start": v(-70, 90) * mm, "end": v(70, 90) * mm});
            skArc(sketch, "E79.3", {"start": v(-70, 90) * mm, "mid": v(-77.07, 87.07) * mm, "end": v(-80, 80) * mm});
            skLineSegment(sketch, "E79.4", {"start": v(80, -80) * mm, "end": v(80, 80) * mm});
            skCircle(sketch, "E79.5", {"center": v(60, 67.5) * mm, "radius": 4 * mm});
            skArc(sketch, "E79.6", {"start": v(80, 80) * mm, "mid": v(77.07, 87.07) * mm, "end": v(70, 90) * mm});
            skArc(sketch, "E79.7", {"start": v(70, -90) * mm, "mid": v(77.07, -87.07) * mm, "end": v(80, -80) * mm});
            skCircle(sketch, "E79.8", {"center": v(60, -67.5) * mm, "radius": 4 * mm});
            skLineSegment(sketch, "E79.9", {"start": v(-70, -90) * mm, "end": v(70, -90) * mm});
            skArc(sketch, "E79.11", {"start": v(-80, -80) * mm, "mid": v(-77.07, -87.07) * mm, "end": v(-70, -90) * mm});
            skLineSegment(sketch, "E80", {"start": v(-33, 90) * mm, "end": v(-15, 108) * mm});
            skLineSegment(sketch, "E81", {"start": v(15, 108) * mm, "end": v(33, 90) * mm});
            skLineSegment(sketch, "E82", {"start": v(-15, 108) * mm, "end": v(-15, 120) * mm});
            skLineSegment(sketch, "E83", {"start": v(15, 108) * mm, "end": v(15, 120) * mm});
            skArc(sketch, "E84", {"start": v(15, 120) * mm, "mid": v(0, 135) * mm, "end": v(-15, 120) * mm});
            skCircle(sketch, "E85", {"center": v(0, 120) * mm, "radius": 6 * mm});
            skLineSegment(sketch, "E86", {"start": v(0, 90) * mm, "end": v(0, 120) * mm, "construction": true});
            skLineSegment(sketch, "E87", {"start": v(-80, 0) * mm, "end": v(80, 0) * mm, "construction": true});
            skArc(sketch, "E88.MirrorCS", {"start": v(15, -120) * mm, "mid": v(0, -135) * mm, "end": v(-15, -120) * mm});
            skCircle(sketch, "E89.MirrorC", {"center": v(0, -120) * mm, "radius": 6 * mm});
            skLineSegment(sketch, "E90.MirrorCS", {"start": v(15, -108) * mm, "end": v(15, -120) * mm});
            skLineSegment(sketch, "E91.MirrorCS", {"start": v(-15, -108) * mm, "end": v(-15, -120) * mm});
            skLineSegment(sketch, "E92.MirrorCS", {"start": v(-33, -90) * mm, "end": v(-15, -108) * mm});
            skLineSegment(sketch, "E93.MirrorCS", {"start": v(15, -108) * mm, "end": v(33, -90) * mm});
            skSolve(sketch);
        }
        {
            var Q0;
            Q0=makeQuery(id+"F16.imprint","IMPRINT",FACE,{"disambiguationData":[TD([[makeQuery(id+"F16.imprint","IMPRINT",EDGE,{"derivedFrom":sQuery(id+"F16.wireOp",EDGE,"E88.MirrorCS")}),-1.0]])]});
            var Q1;
            Q1=makeQuery(id+"F16.imprint","IMPRINT",FACE,{"disambiguationData":[TD([[makeQuery(id+"F16.imprint","IMPRINT",EDGE,{"derivedFrom":sQuery(id+"F16.wireOp",EDGE,"E79.0")}),-1.0]])]});
            var Q2;
            {var subQ1=sQuery(id+"F16.wireOp",EDGE,"E80");Q2=makeQuery(id+"F16.imprint","IMPRINT",FACE,{"disambiguationData":[TD([[makeQuery(id+"F16.imprint","IMPRINT",EDGE,{"derivedFrom":subQ1}),-1.0]])]});}
            var Q3;
            Q3=makeQuery(id+"F2.opExtrude","CAP_FACE",FACE,{"disambiguationData":[OSD([sQuery(id+"F0.wireOp",EDGE,"E12"),sQuery(id+"F0.wireOp",EDGE,"E13"),sQuery(id+"F0.wireOp",EDGE,"E14"),sQuery(id+"F0.wireOp",EDGE,"E15"),sQuery(id+"F0.wireOp",EDGE,"E17.filletArc"),sQuery(id+"F0.wireOp",EDGE,"E18.filletArc"),sQuery(id+"F0.wireOp",EDGE,"E19.filletArc"),sQuery(id+"F0.wireOp",EDGE,"E20.filletArc"),sQuery(id+"F0.wireOp",EDGE,"E25.0"),sQuery(id+"F0.wireOp",EDGE,"E25.1"),sQuery(id+"F0.wireOp",EDGE,"E25.2"),sQuery(id+"F0.wireOp",EDGE,"E25.3"),sQuery(id+"F0.wireOp",EDGE,"E25.4"),sQuery(id+"F0.wireOp",EDGE,"E25.5"),sQuery(id+"F0.wireOp",EDGE,"E25.6"),sQuery(id+"F0.wireOp",EDGE,"E25.7")])],"isStart":false});
            extrude(context, id + "F17", {"entities" : qUnion([Q0, Q1, Q2]), "endBound" : BoundingType.UP_TO_SURFACE, "depth" : 25 * mm, "endBoundEntityFace" : qUnion([Q3]), "offsetDistance" : 25 * mm});
        }
    });
